# Revit family: AFX-Apex-Flush_Mount
name_source: partatom
category: Lighting Fixtures
units: mm (PartAtom-declared; Revit-internal decimal feet)

## family parameters
Cut with Voids When Loaded = No
Host = Face
Light Source = Yes
Part Type = Normal
Room Calculation Point = No
Round Connector Dimension = Use Diameter
Shared = No

## types (5) — shared parameters
Apparent Load = 0 VA
Assembly Code = D5020200
Color Filter = 16777215
Colour Rendering Index = 80
Default Elevation = 48"
Diffuser Finish = AFX - White Acrylic
Dimming Lamp Color Temperature Shift = <None>
Emit Shape Visible in Rendering = No
Housing Finish = AFX - Black Steel
Keynote = 12500
Manufacturer = AFX Inc
Power Factor = 1
Product Documentation Link = https://www.afxinc.com
Revit File Built By = https://servex-us.com
Supports Finish = AFX - Wood
Sustainability = https://lamprecycle.org
Tilt Angle = 90.00°
Type Comments = Apex
URL = https://www.afxinc.com
Voltage = 120 V
Wattage Comments = 9

## per-type parameters (varying)
| type | Description | Diameter | Dist SU | Emit from Circle Diameter | H SU | Height | Photometric Web File |
| APF1214LAJUDES | Led Flush Mount - 14 1/4"Dia x 4 1/4"H | 14 1/4" | 7 1/8" | 12" | 3 7/8" | 4 1/4" | APF1524LAJxxxx-LW.ies |
| APF1524LAJUDES | Led Flush Mount - 17"Dia x 4 1/4"H | 17" | 8 1/2" | 15" | 3 7/8" | 4 1/4" | APF1524LAJxxxx-LW.ies |
| APF1932LAJUDES | Led Flush Mount - 21 1/4"Dia x 4 1/4"H | 21 1/4" | 10 5/8" | 18" | 3 7/8" | 4 1/4" | APF1932LAJxxxx-LW.ies |
| APF2432L5AJUDES | Led Flush Mount - 27 1/4"Dia x 6"H | 27 1/4" | 13 5/8" | 24" | 5 45/64" | 6" | APF1932LAJxxxx-LW.ies |
| APF3044L5AJUDES | Led Flush Mount - 33 3/8"Dia x 7 1/4"H | 33 3/8" | 16 11/16" | 30" | 6 61/64" | 7 1/4" | APF1932LAJxxxx-LW.ies |

note: column(s) folded — value = type name in every type: Model

## geometry (parser evidence)
native form markers: Sweep x4
no freeform markers — native parametric forms only
